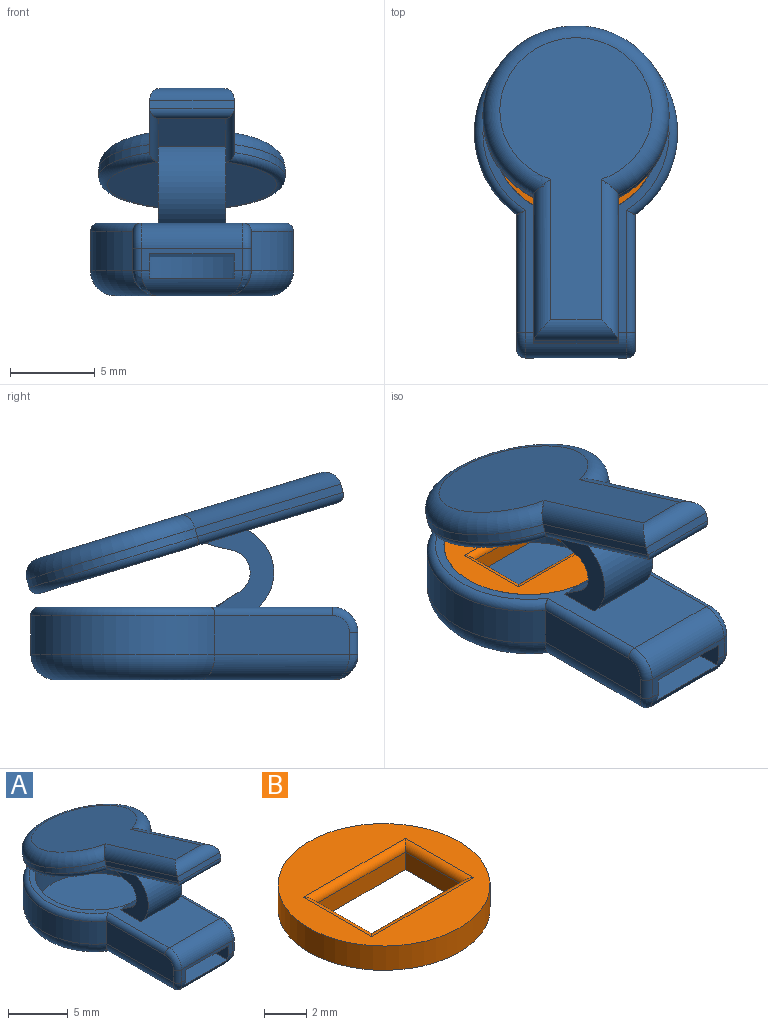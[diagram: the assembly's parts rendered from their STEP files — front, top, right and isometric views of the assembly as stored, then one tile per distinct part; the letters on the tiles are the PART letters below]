
ASSEMBLY  parts=2 mates=1
PART A: 47 faces, bbox 13.3x20.4x12.8 mm
  f0: plane 5.36x4mm, normal (0,-0.29,-0.96), area 22.4mm2, adj f35,f36,f38,f43
  f1: plane 10x9.77mm, normal (0,-0.29,-0.96), area 80mm2, adj f35,f37,f38,f46
  f2: plane 9x1.5mm, normal (-1,0,0), area 11.8mm2, adj f4,f5,f11,f12,f16,f27
  f3: plane 9x1.5mm, normal (1,0,0), area 11.8mm2, adj f4,f5,f11,f12,f16,f27
  f4: plane 6x1.3mm, normal (0,-1,0), area 2.8mm2, adj f2,f3,f5,f17,f19,f25,f27
  f5: cylinder r=1.5mm len=6mm, axis (-1,0,0), area 9.2mm2, adj f2,f3,f4,f10,f12,f18,f26
  f6: plane 17.62x11.29mm, normal (0,0,1), area 46.3mm2, adj f11,f17,f21,f22,f23,f28,f29,f43
  f7: plane 7.96x2.3mm, normal (1,0,0), area 18.1mm2, adj f8,f15,f23,f24,f25
  f8: cylinder r=6mm len=12mm, axis (0,0,1), area 69.5mm2, adj f7,f9,f13,f22
  f9: plane 7.96x2.3mm, normal (-1,0,0), area 18.1mm2, adj f8,f14,f19,f20,f21
  f10: plane 16.33x9mm, normal (0,0,-1), area 93.5mm2, adj f5,f13,f14,f15
  f11: cylinder r=5mm len=10mm, axis (0,0,1), area 96.9mm2, adj f2,f3,f6,f12,f16,f45
  f12: plane 18.24x10mm, normal (0,0,1), area 120.8mm2, adj f2,f3,f5,f11
  f13: torus R=4.5mm, axis (0,0,1), area 66.7mm2, adj f8,f10,f14,f15
  f14: cylinder r=1.5mm len=8.8mm, axis (0,1,0), area 18.6mm2, adj f9,f10,f13,f18
  f15: cylinder r=1.5mm len=8.8mm, axis (0,-1,0), area 18.6mm2, adj f7,f10,f13,f26
  f16: plane 7.5x5mm, normal (0,0,-1), area 35.2mm2, adj f2,f3,f11,f27
  f17: cylinder r=1.5mm len=6mm, axis (1,0,0), area 14.1mm2, adj f4,f6,f20,f24
  f18: bspline ~1.76x1.5mm, area 0.8mm2, adj f5,f14,f19
  f19: cylinder r=0.5mm len=1.3mm, axis (0,0,1), area 1mm2, adj f4,f9,f18,f20
  f20: torus R=1mm, axis (-1,0,0), area 1.6mm2, adj f9,f17,f19,f21
  f21: cylinder r=0.5mm len=7.22mm, axis (0,-1,0), area 5.6mm2, adj f6,f9,f20,f22
  f22: torus R=5.5mm, axis (0,0,1), area 23.2mm2, adj f6,f8,f21,f23
  f23: cylinder r=0.5mm len=7.22mm, axis (0,1,0), area 5.6mm2, adj f6,f7,f22,f24
  f24: torus R=1mm, axis (-1,0,0), area 1.6mm2, adj f7,f17,f23,f25
  f25: cylinder r=0.5mm len=1.3mm, axis (0,0,-1), area 1mm2, adj f4,f7,f24,f26
  f26: bspline ~1.57x1.5mm, area 0.8mm2, adj f5,f15,f25
  f27: plane 5x1.5mm, normal (0,-0.13,-0.99), area 7.6mm2, adj f2,f3,f4,f16
  f28: plane 4.6x4.13mm, normal (-1,0,0), area 8.3mm2, adj f6,f35,f43,f44,f45,f46
  f29: plane 4.6x4.13mm, normal (1,0,0), area 8.3mm2, adj f6,f38,f43,f44,f45,f46
  f30: cylinder r=5.5mm len=11mm, axis (0,-0.29,-0.96), area 14.7mm2, adj f31,f33,f37,f41
  f31: plane 8.76x3.1mm, normal (1,0,0), area 4.5mm2, adj f30,f32,f38,f42
  f32: plane 5x0.48mm, normal (0,-0.96,0.29), area 2.5mm2, adj f31,f33,f36,f40
  f33: plane 8.76x3.1mm, normal (-1,0,0), area 4.5mm2, adj f30,f32,f35,f39
  f34: plane 16.65x9mm, normal (0,0.29,0.96), area 89.1mm2, adj f39,f40,f41,f42
  f35: cylinder r=0.5mm len=9.06mm, axis (0,0.96,-0.29), area 7mm2, adj f0,f1,f28,f33,f36,f37
  f36: cylinder r=0.5mm len=5mm, axis (-1,0,0), area 3.5mm2, adj f0,f32,f35,f38
  f37: torus R=5mm, axis (0,-0.29,-0.96), area 22.6mm2, adj f1,f30,f35,f38
  f38: cylinder r=0.5mm len=9.06mm, axis (0,-0.96,0.29), area 7mm2, adj f0,f1,f29,f31,f36,f37
  f39: cylinder r=1mm len=9.53mm, axis (0,-0.96,0.29), area 13.9mm2, adj f33,f34,f40,f41
  f40: cylinder r=1mm len=5mm, axis (1,0,0), area 6.3mm2, adj f32,f34,f39,f42
  f41: torus R=4.5mm, axis (0,-0.29,-0.96), area 44.1mm2, adj f30,f34,f39,f42
  f42: cylinder r=1mm len=9.53mm, axis (0,0.96,-0.29), area 13.9mm2, adj f31,f34,f40,f41
  f43: cylinder r=2.75mm len=4.53mm, axis (-1,0,0), area 21.7mm2, adj f0,f6,f28,f29
  f44: cylinder r=1.35mm len=4mm, axis (-1,0,0), area 13.2mm2, adj f28,f29,f45,f46
  f45: bspline ~5.2x2.06mm, area 6.2mm2, adj f6,f11,f28,f29,f44
  f46: cylinder r=10mm len=4mm, axis (1,0,0), area 6.5mm2, adj f1,f28,f29,f44
PART B: 11 faces, bbox 10x10x1.4 mm
  f0: plane 3.75x1mm, normal (1,0,0), area 3.8mm2, adj f1,f4,f5,f7
  f1: plane 6x1mm, normal (0,-1,0), area 6mm2, adj f0,f2,f5,f8
  f2: plane 3.75x1mm, normal (-1,0,0), area 3.8mm2, adj f1,f4,f5,f10
  f3: cylinder r=5mm len=10mm, axis (0,0,1), area 44mm2, adj f5,f6
  f4: plane 6x1mm, normal (0,1,0), area 6mm2, adj f0,f2,f5,f9
  f5: plane 10x10mm, normal (0,0,-1), area 56mm2, adj f0,f1,f2,f3,f4
  f6: plane 10x10mm, normal (0,0,1), area 47.6mm2, adj f3,f7,f8,f9,f10
  f7: cylinder r=0.4mm len=4.55mm, axis (0,1,0), area 2.5mm2, adj f0,f6,f8,f9
  f8: cylinder r=0.4mm len=6.8mm, axis (1,0,0), area 4mm2, adj f1,f6,f7,f10
  f9: cylinder r=0.4mm len=6.8mm, axis (-1,0,0), area 4mm2, adj f4,f6,f7,f10
  f10: cylinder r=0.4mm len=4.55mm, axis (0,-1,0), area 2.5mm2, adj f2,f6,f8,f9
PLACE A t=(18.01,-1.36,0.15)mm
PLACE B t=(18.01,-1.36,0.15)mm
MATE slider B.f3 <-> A.f8  axis (0,0,1) through (18.01,-1.36,0.15)mm
